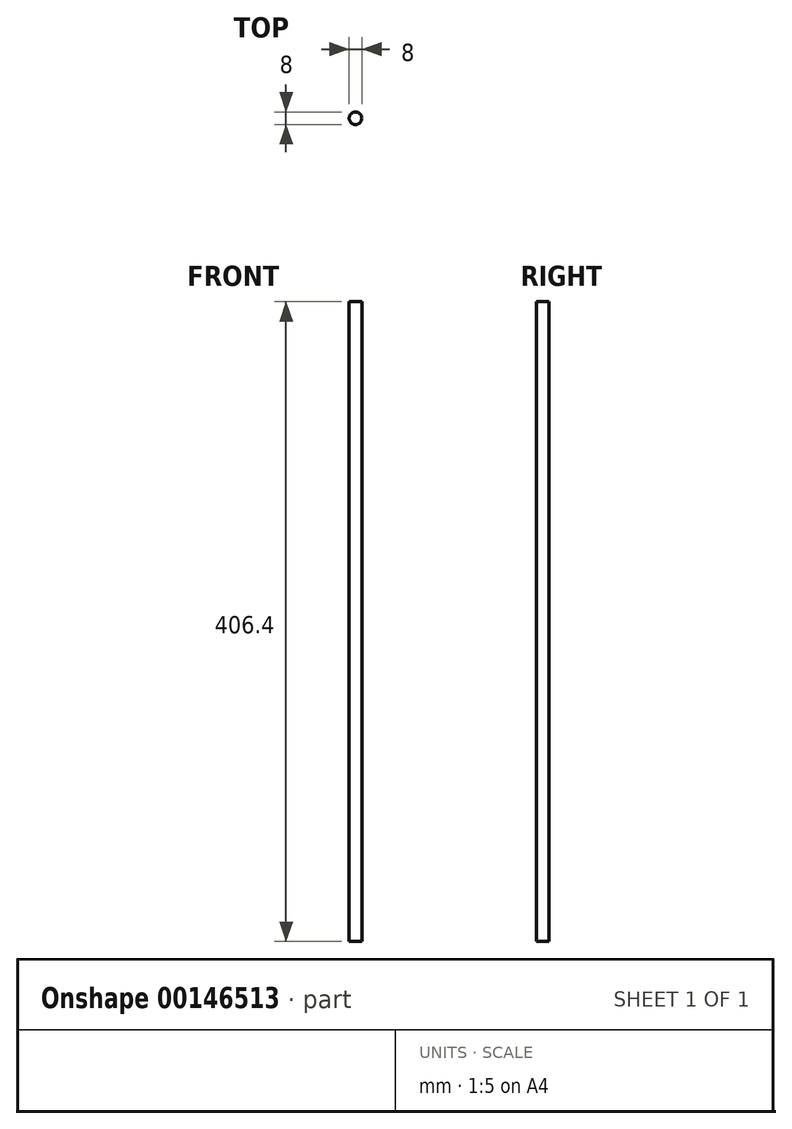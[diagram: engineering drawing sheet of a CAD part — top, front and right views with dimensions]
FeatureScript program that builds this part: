
annotation { "Feature Type Name" : "Feature", "Feature Type Description" : "" }
export const myFeature = defineFeature(function(context is Context, id is Id, definition is map)
    precondition{}
    {
        {
            var Q0;
            Q0=qCreatedBy(makeId("Top.planeOp"),FACE);
            var sketch = newSketch(context, id + "F0", { "sketchPlane" : qUnion([Q0])});
            skCircle(sketch, "E0", {"center": v(0, 0) * mm, "radius": 4 * mm});
            skSolve(sketch);
        }
        {
            var Q0;
            Q0 = qSketchRegion(id + "F0", true);
            extrude(context, id + "F1", {"entities" : qUnion([Q0]), "depth" : 406.4 * mm});
        }
    });
